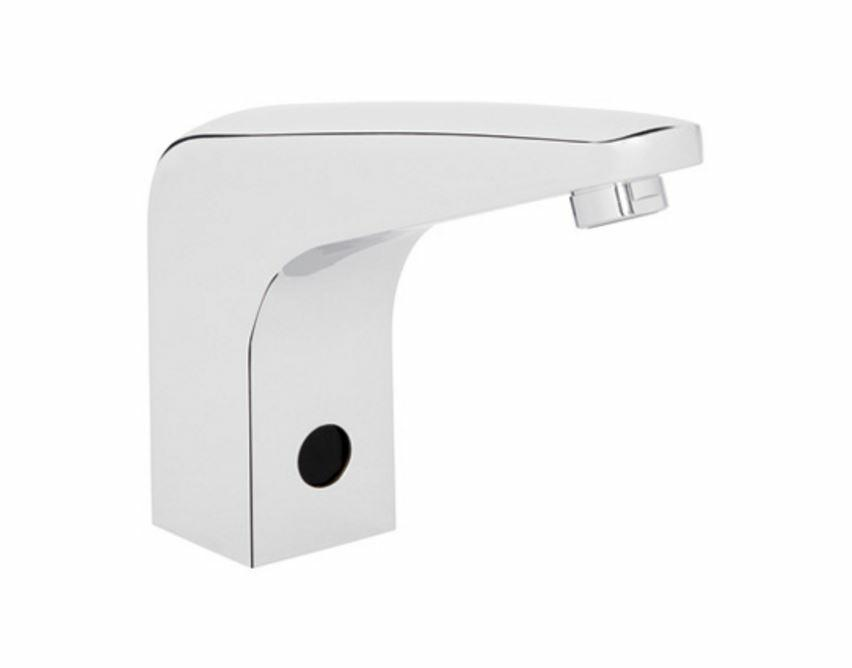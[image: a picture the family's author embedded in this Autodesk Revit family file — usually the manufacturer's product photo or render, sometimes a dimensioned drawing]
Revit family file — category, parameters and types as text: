
# Revit family: TV-304-C
name_source: partatom
category: Aparatos sanitarios
units: mm (PartAtom-declared; Revit-internal decimal feet)

## family parameters
Compartido = Sí
Corte con vacíos al cargar = No
Cota de conector redondo = Diámetro de uso
Número OmniClass = 23.45.55.14
Punto de cálculo de habitación = Sí
Se basa en plano de trabajo = No
Siempre vertical = Sí
Tipo de pieza = Normal
Título OmniClass = Single Faucets

## types (1)
- TV-304-C
    Accesorios = Llave hexagonal 1-1/16", Kit de sujeción, Módulo electrónico
    Chrome = Brass Chromed
    Comentarios de tipo = Línea Electrónica
    Conexión AF = Sí
    Connection = ½" - 14 NPSM
    Descripción = Llave electrónica de sensor de corriente.
    Detection Range = 9.8" (25 cm)
    Elevación por defecto = 0 "
    Fabricante = Helvex
    Features = Sensor infrarrojo, Distancia de detección 25cm (ajuste de fábrica), Fuente de alimentación regulada clase 2, Entrada: 115 - 230 Vca, 50/60 Hz, Salida: 6V cc/200mA
    Feeding Voltage = 6 V
    Imagen de tipo = TV-304.JPG
    Max. Working Pressure = 85.3 psi
    Min. Working Pressure = 11.3 psi
    Modelo = TV-304-C
    Operación = Active la salida colocando su mano dentro de la
zona de detección.

## geometry (parser evidence)
native form markers: Sweep x3
no freeform markers — native parametric forms only
